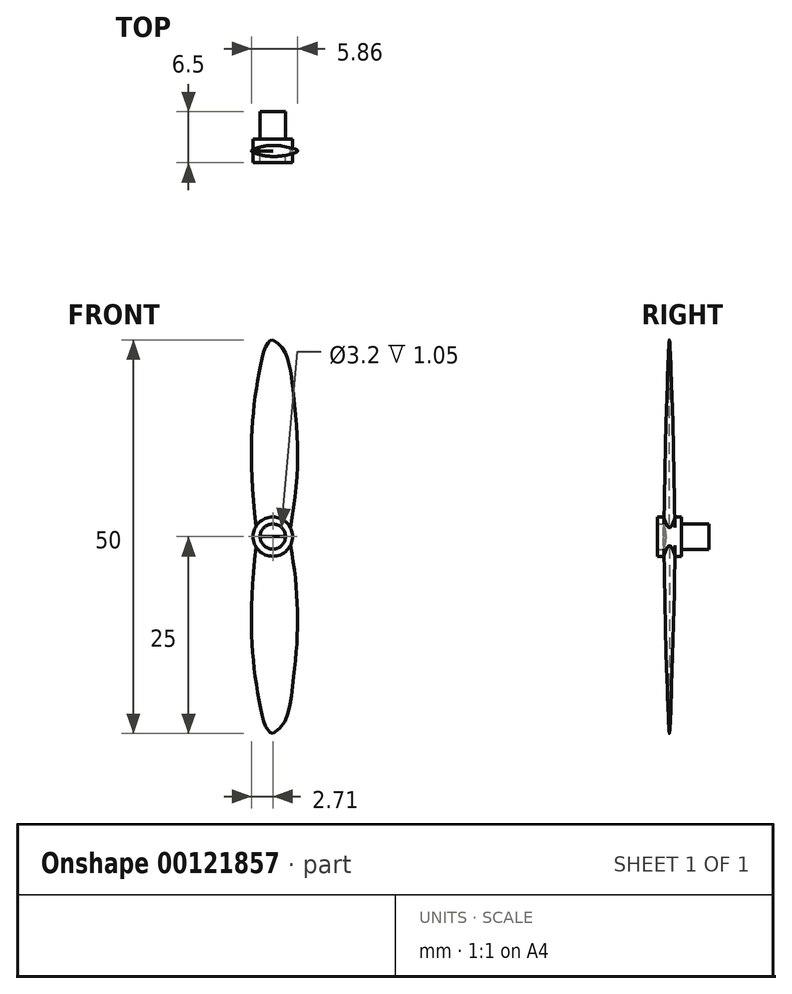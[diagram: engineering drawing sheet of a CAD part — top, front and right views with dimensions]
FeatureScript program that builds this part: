
annotation { "Feature Type Name" : "Feature", "Feature Type Description" : "" }
export const myFeature = defineFeature(function(context is Context, id is Id, definition is map)
    precondition{}
    {
        {
            var Q0;
            Q0=qCreatedBy(makeId("Top.planeOp"),FACE);
            var sketch = newSketch(context, id + "F0", { "sketchPlane" : qUnion([Q0])});
            skEllipse(sketch, "E0", {"center": v(0, 0) * mm, "majorRadius": 2 * mm, "minorRadius": 0.75 * mm, "majorAxis": v(1, 0)});
            skPoint(sketch, "E1", {"position": v(-2, 0) * mm});
            skPoint(sketch, "E2", {"position": v(2, 0) * mm});
            skSolve(sketch);
        }
        {
            var Q0;
            Q0=qCreatedBy(makeId("Top.planeOp"),FACE);
            cPlane(context, id + "F1", {"entities" : qUnion([Q0]), "cplaneType" : CPlaneType.OFFSET, "offset" : 25 * mm, "oppositeDirection" : true, "width" : 150 * mm, "height" : 150 * mm});
        }
        {
            var Q0;
            Q0=qCreatedBy(id+"F1.planeOp",FACE);
            var sketch = newSketch(context, id + "F2", { "sketchPlane" : qUnion([Q0])});
            skPoint(sketch, "E3", {"position": v(0, 0) * mm});
            skSolve(sketch);
        }
        {
            var Q0;
            Q0=sQuery(id+"F0.wireOp",VERTEX,"E1");
            var Q1;
            Q1=sQuery(id+"F0.wireOp",VERTEX,"E2");
            var Q2;
            Q2=sQuery(id+"F2.wireOp",VERTEX,"E3");
            cPlane(context, id + "F3", {"entities" : qUnion([Q0, Q1, Q2]), "cplaneType" : CPlaneType.THREE_POINT, "offset" : 25 * mm, "width" : 150 * mm, "height" : 150 * mm});
        }
        {
            var Q0;
            Q0=qCreatedBy(id+"F3.planeOp",FACE);
            var sketch = newSketch(context, id + "F4", { "sketchPlane" : qUnion([Q0])});
            skFitSpline(sketch, "E4", {"points": [v(-2, 0) * mm, v(-2.03, -19.26) * mm, v(0, -25) * mm], "startDerivative": vector(-4.97, -43.31) * mm, "endDerivative": vector(8.22, 0.38) * mm});
            skFitSpline(sketch, "E5", {"points": [v(0, -25) * mm, v(2.47, -19.34) * mm, v(2, 0) * mm], "startDerivative": vector(16.1, 8.83) * mm, "endDerivative": vector(-8.77, 41.12) * mm});
            skSolve(sketch);
        }
        {
            var Q0;
            Q0=makeQuery(id+"F0.imprint","IMPRINT",FACE,{"disambiguationData":[TD([[makeQuery(id+"F0.imprint","IMPRINT",EDGE,{"derivedFrom":sQuery(id+"F0.wireOp",EDGE,"E0")}),1.0]])]});
            var Q1;
            Q1=sQuery(id+"F2.wireOp",VERTEX,"E3");
            var Q2;
            Q2=sQuery(id+"F4.wireOp",EDGE,"E4");
            var Q3;
            Q3=sQuery(id+"F4.wireOp",EDGE,"E5");
            loft(context, id + "F5", {"addGuides" : true, "sheetProfilesArray" : [{ "sheetProfileEntities" : qUnion([Q0]) }, { "sheetProfileEntities" : qUnion([Q1]) }], "guidesArray" : [{ "guideEntities" : qUnion([Q2]), "guideDerivativeType" : LoftGuideDerivativeType.DEFAULT, "guideDerivativeMagnitude" : 1 }, { "guideEntities" : qUnion([Q3]), "guideDerivativeType" : LoftGuideDerivativeType.DEFAULT, "guideDerivativeMagnitude" : 1 }]});
        }
        {
            var Q0;
            Q0=qCreatedBy(makeId("Front.planeOp"),FACE);
            var sketch = newSketch(context, id + "F6", { "sketchPlane" : qUnion([Q0])});
            skCircle(sketch, "E6", {"center": v(0, 0) * mm, "radius": 1.6 * mm});
            skCircle(sketch, "E7", {"center": v(0, 0) * mm, "radius": 2.5 * mm});
            skSolve(sketch);
        }
        {
            var Q0;
            Q0=makeQuery(id+"F5.opLoft","SWEPT_BODY",BODY,{"disambiguationData":[OSD([makeQuery(id+"F0.imprint","IMPRINT",FACE,{"disambiguationData":[TD([[makeQuery(id+"F0.imprint","IMPRINT",EDGE,{"derivedFrom":sQuery(id+"F0.wireOp",EDGE,"E0")}),1.0]])]}),sQuery(id+"F2.wireOp",VERTEX,"E3"),sQuery(id+"F4.wireOp",EDGE,"E4"),sQuery(id+"F4.wireOp",EDGE,"E5")])]});
            var Q1;
            Q1=qCreatedBy(makeId("Top.planeOp"),FACE);
            mirror(context, id + "F7", {"operationType" : NewBodyOperationType.ADD, "entities" : qUnion([Q0]), "mirrorPlane" : qUnion([Q1])});
        }
        {
            var Q0;
            Q0 = qSketchRegion(id + "F6", true);
            extrude(context, id + "F8", {"entities" : qUnion([Q0]), "operationType" : NewBodyOperationType.ADD, "endBound" : BoundingType.SYMMETRIC, "depth" : 3 * mm, "offsetDistance" : 25 * mm});
        }
        {
            var Q0;
            Q0=makeQuery(id+"F6.imprint","IMPRINT",FACE,{"disambiguationData":[TD([[makeQuery(id+"F6.imprint","IMPRINT",EDGE,{"derivedFrom":sQuery(id+"F6.wireOp",EDGE,"E6")}),1.0]])]});
            extrude(context, id + "F9", {"entities" : qUnion([Q0]), "operationType" : NewBodyOperationType.ADD, "oppositeDirection" : true, "depth" : 5 * mm, "offsetDistance" : 25 * mm});
        }
    });
